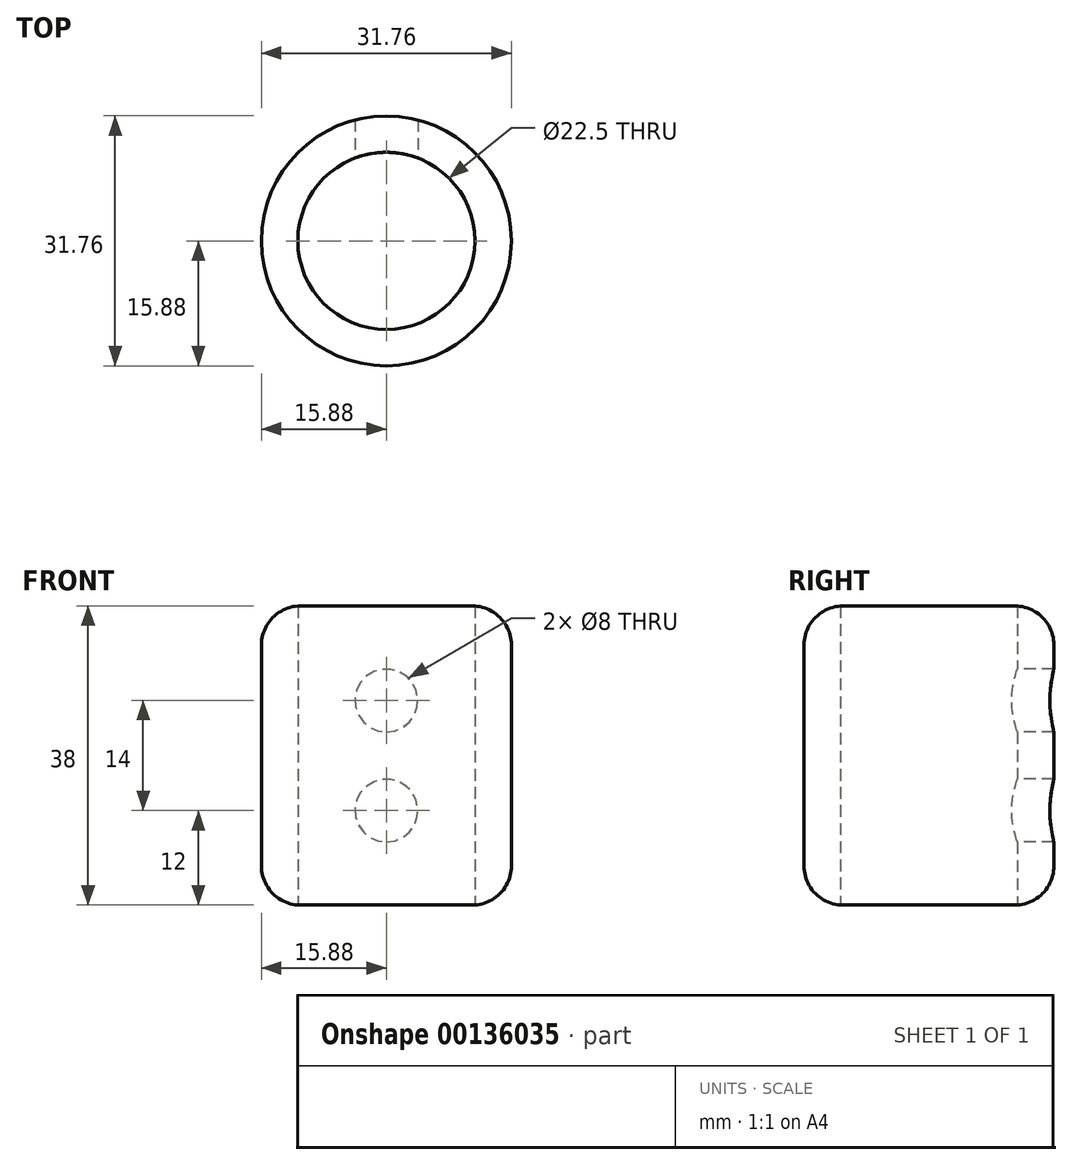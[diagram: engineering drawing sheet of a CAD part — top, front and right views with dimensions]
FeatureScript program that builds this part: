
annotation { "Feature Type Name" : "Feature", "Feature Type Description" : "" }
export const myFeature = defineFeature(function(context is Context, id is Id, definition is map)
    precondition{}
    {
        {
            var Q0;
            Q0=qCreatedBy(makeId("Top.planeOp"),FACE);
            var sketch = newSketch(context, id + "F0", { "sketchPlane" : qUnion([Q0])});
            skCircle(sketch, "E0", {"center": v(0, 0) * mm, "radius": 11.25 * mm});
            skCircle(sketch, "E1", {"center": v(0, 0) * mm, "radius": 15.88 * mm});
            skSolve(sketch);
        }
        {
            var Q0;
            Q0 = qSketchRegion(id + "F0", true);
            extrude(context, id + "F1", {"entities" : qUnion([Q0]), "depth" : 38 * mm});
        }
        {
            var Q0;
            Q0=makeQuery(id+"F1.opExtrude","CAP_EDGE",EDGE,{"disambiguationData":[OSD([sQuery(id+"F0.wireOp",EDGE,"E1")])],"isStart":false});
            var Q1;
            Q1=makeQuery(id+"F1.opExtrude","CAP_EDGE",EDGE,{"disambiguationData":[OSD([sQuery(id+"F0.wireOp",EDGE,"E1")])],"isStart":true});
            fillet(context, id + "F2", {"entities" : qUnion([Q0, Q1]), "radius" : 5 * mm, "tangentPropagation" : true, "allowEdgeOverflow" : false});
        }
        {
            var Q0;
            Q0=qCreatedBy(makeId("Front.planeOp"),FACE);
            var sketch = newSketch(context, id + "F3", { "sketchPlane" : qUnion([Q0])});
            skLineSegment(sketch, "E2", {"start": v(0, 0) * mm, "end": v(0, 38) * mm, "construction": true});
            skLineSegment(sketch, "E3", {"start": v(0, 38) * mm, "end": v(10, 38) * mm, "construction": true});
            skLineSegment(sketch, "E4", {"start": v(0, 0) * mm, "end": v(10, 0) * mm});
            skLineSegment(sketch, "E5.0", {"start": v(0, 19) * mm, "end": v(10, 19) * mm, "construction": true});
            skLineSegment(sketch, "E6.0", {"start": v(0, 12) * mm, "end": v(10, 12) * mm});
            skLineSegment(sketch, "E7.0", {"start": v(0, 26) * mm, "end": v(10, 26) * mm});
            skCircle(sketch, "E8", {"center": v(0, 12) * mm, "radius": 4 * mm});
            skCircle(sketch, "E9", {"center": v(0, 26) * mm, "radius": 4 * mm});
            skSolve(sketch);
        }
        {
            var Q0;
            Q0 = qSketchRegion(id + "F3", true);
            extrude(context, id + "F4", {"entities" : qUnion([Q0]), "operationType" : NewBodyOperationType.REMOVE, "endBound" : BoundingType.THROUGH_ALL, "oppositeDirection" : true, "depth" : 25 * mm});
        }
    });
